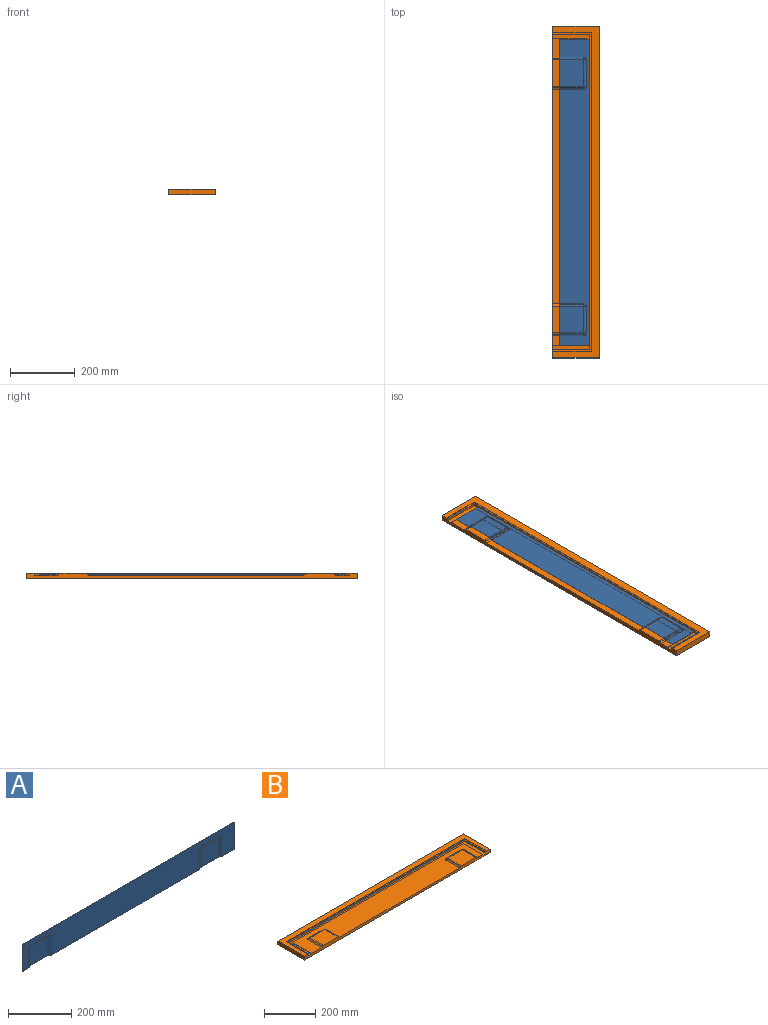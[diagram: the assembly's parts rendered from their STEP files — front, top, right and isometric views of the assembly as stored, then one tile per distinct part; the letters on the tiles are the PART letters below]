
ASSEMBLY  parts=2 mates=1
PART A: 50 faces, bbox 946.3x6.2x105 mm
  f0: plane 105x0.75mm, normal (-1,0,0), area 78.8mm2, adj f1,f2,f3,f4
  f1: plane 946.3x105mm, normal (0,1,0), area 82973.2mm2, adj f0,f2,f4,f5,f6,f7,f8,f9
  f2: plane 946.3x6.15mm, normal (0,0,-1), area 715.9mm2, adj f0,f1,f3,f5,f6,f10,f11,f15
  f3: plane 946.3x105mm, normal (0,-1,0), area 82973.2mm2, adj f0,f2,f4,f5,f29,f33,f34,f37
  f4: plane 946.3x0.75mm, normal (0,0,1), area 709.7mm2, adj f0,f1,f3,f5
  f5: plane 105x0.75mm, normal (1,0,0), area 78.8mm2, adj f1,f2,f3,f4
  f6: cylinder r=5mm len=73.6mm, axis (0,0,-1), area 402.2mm2, adj f1,f2,f7,f21
  f7: torus R=8.88mm, axis (0,-1,0), area 55mm2, adj f1,f6,f8,f22
  f8: cylinder r=5mm len=82mm, axis (-1,0,0), area 448mm2, adj f1,f7,f9,f23
  f9: torus R=8.88mm, axis (0,-1,0), area 55mm2, adj f1,f8,f10,f24
  f10: cylinder r=5mm len=73.6mm, axis (0,0,1), area 402.2mm2, adj f1,f2,f9,f19
  f11: cylinder r=5mm len=73.6mm, axis (0,0,-1), area 402.2mm2, adj f1,f2,f12,f18
  f12: torus R=8.88mm, axis (0,-1,0), area 55mm2, adj f1,f11,f13,f25
  f13: cylinder r=5mm len=82mm, axis (-1,0,0), area 448mm2, adj f1,f12,f14,f26
  f14: torus R=8.88mm, axis (0,-1,0), area 55mm2, adj f1,f13,f15,f27
  f15: cylinder r=5mm len=73.6mm, axis (0,0,1), area 402.2mm2, adj f1,f2,f14,f16
  f16: cylinder r=5mm len=73.6mm, axis (0,0,-1), area 402.2mm2, adj f2,f15,f17,f27
  f17: plane 82x73.6mm, normal (0,1,0), area 6035.2mm2, adj f2,f16,f18,f26
  f18: cylinder r=5mm len=73.6mm, axis (0,0,1), area 402.2mm2, adj f2,f11,f17,f25
  f19: cylinder r=5mm len=73.6mm, axis (0,0,-1), area 402.2mm2, adj f2,f10,f20,f24
  f20: plane 82x73.6mm, normal (0,1,0), area 6035.2mm2, adj f2,f19,f21,f23
  f21: cylinder r=5mm len=73.6mm, axis (0,0,1), area 402.2mm2, adj f2,f6,f20,f22
  f22: sphere r=5mm, area 21.2mm2, adj f7,f21,f23
  f23: cylinder r=5mm len=82mm, axis (-1,0,0), area 448mm2, adj f8,f20,f22,f24
  f24: sphere r=5mm, area 21.2mm2, adj f9,f19,f23
  f25: sphere r=5mm, area 21.2mm2, adj f12,f18,f26
  f26: cylinder r=5mm len=82mm, axis (-1,0,0), area 448mm2, adj f13,f17,f25,f27
  f27: sphere r=5mm, area 21.2mm2, adj f14,f16,f26
  f28: cylinder r=4.25mm len=82mm, axis (-1,0,0), area 380.8mm2, adj f29,f30,f31,f32
  f29: cylinder r=5.75mm len=82mm, axis (-1,0,0), area 515.3mm2, adj f3,f28,f33,f34
  f30: sphere r=4.25mm, area 15.3mm2, adj f28,f33,f35
  f31: plane 82x73.6mm, normal (0,-1,0), area 6035.2mm2, adj f2,f28,f35,f36
  f32: sphere r=4.25mm, area 15.3mm2, adj f28,f34,f36
  f33: torus R=8.88mm, axis (0,-1,0), area 59.6mm2, adj f3,f29,f30,f37
  f34: torus R=8.88mm, axis (0,-1,0), area 59.6mm2, adj f3,f29,f32,f38
  f35: cylinder r=4.25mm len=73.6mm, axis (0,0,-1), area 341.8mm2, adj f2,f30,f31,f37
  f36: cylinder r=4.25mm len=73.6mm, axis (0,0,1), area 341.8mm2, adj f2,f31,f32,f38
  f37: cylinder r=5.75mm len=73.6mm, axis (0,0,1), area 462.5mm2, adj f2,f3,f33,f35
  f38: cylinder r=5.75mm len=73.6mm, axis (0,0,-1), area 462.5mm2, adj f2,f3,f34,f36
  f39: cylinder r=4.25mm len=82mm, axis (-1,0,0), area 380.8mm2, adj f40,f41,f42,f43
  f40: cylinder r=5.75mm len=82mm, axis (-1,0,0), area 515.3mm2, adj f3,f39,f44,f45
  f41: sphere r=4.25mm, area 15.3mm2, adj f39,f45,f46
  f42: plane 82x73.6mm, normal (0,-1,0), area 6035.2mm2, adj f2,f39,f46,f47
  f43: sphere r=4.25mm, area 15.3mm2, adj f39,f44,f47
  f44: torus R=8.88mm, axis (0,-1,0), area 59.6mm2, adj f3,f40,f43,f48
  f45: torus R=8.88mm, axis (0,-1,0), area 59.6mm2, adj f3,f40,f41,f49
  f46: cylinder r=4.25mm len=73.6mm, axis (0,0,-1), area 341.8mm2, adj f2,f41,f42,f49
  f47: cylinder r=4.25mm len=73.6mm, axis (0,0,1), area 341.8mm2, adj f2,f42,f43,f48
  f48: cylinder r=5.75mm len=73.6mm, axis (0,0,-1), area 462.5mm2, adj f2,f3,f44,f47
  f49: cylinder r=5.75mm len=73.6mm, axis (0,0,1), area 462.5mm2, adj f2,f3,f45,f46
PART B: 40 faces, bbox 1026.3x145x18.4 mm
  f0: plane 976.3x115mm, normal (0,0,1), area 12913mm2, adj f4,f7,f8,f9,f12,f13,f14
  f1: plane 946.3x105mm, normal (0,0,1), area 82966.5mm2, adj f4,f7,f8,f9,f30,f31,f32,f33
  f2: plane 1026.3x18.4mm, normal (0,1,0), area 18883.9mm2, adj f3,f5,f6,f19
  f3: plane 145x18.4mm, normal (-1,0,0), area 2668mm2, adj f2,f4,f6,f19
  f4: plane 1026.3x18.4mm, normal (0,-1,0), area 13541mm2, adj f0,f1,f3,f5,f6,f7,f9,f10
  f5: plane 145x18.4mm, normal (1,0,0), area 2668mm2, adj f2,f4,f6,f19
  f6: plane 1026.3x145mm, normal (0,0,-1), area 148813.5mm2, adj f2,f3,f4,f5
  f7: plane 105x2mm, normal (1,0,0), area 210mm2, adj f0,f1,f4,f8
  f8: plane 946.3x2mm, normal (0,1,0), area 1892.6mm2, adj f0,f1,f7,f9
  f9: plane 105x2mm, normal (-1,0,0), area 210mm2, adj f0,f1,f4,f8
  f10: plane 82x73.6mm, normal (0,0,1), area 6035.2mm2, adj f4,f25,f27,f28
  f11: plane 82x73.6mm, normal (0,0,1), area 6035.2mm2, adj f4,f20,f22,f23
  f12: plane 115x7.4mm, normal (1,0,0), area 851mm2, adj f0,f4,f13,f15
  f13: plane 976.3x7.4mm, normal (0,-1,0), area 7224.6mm2, adj f0,f12,f14,f15
  f14: plane 115x7.4mm, normal (-1,0,0), area 851mm2, adj f0,f4,f13,f15
  f15: plane 986.3x120mm, normal (0,0,1), area 6081.5mm2, adj f4,f12,f13,f14,f16,f17,f18
  f16: plane 120x1mm, normal (1,0,0), area 120mm2, adj f4,f15,f17,f19
  f17: plane 986.3x1mm, normal (0,-1,0), area 986.3mm2, adj f15,f16,f18,f19
  f18: plane 120x1mm, normal (-1,0,0), area 120mm2, adj f4,f15,f17,f19
  f19: plane 1026.3x145mm, normal (0,0,1), area 30457.5mm2, adj f2,f3,f4,f5,f16,f17,f18
  f20: cylinder r=4.25mm len=74.03mm, axis (0,1,0), area 342.8mm2, adj f4,f11,f21,f30
  f21: bspline ~3.98x3.98mm, area 8.1mm2, adj f20,f22,f31
  f22: cylinder r=4.25mm len=82.85mm, axis (-1,0,0), area 382.8mm2, adj f11,f21,f24,f33
  f23: cylinder r=4.25mm len=74.03mm, axis (0,1,0), area 342.8mm2, adj f4,f11,f24,f32
  f24: bspline ~3.98x3.98mm, area 8.1mm2, adj f22,f23,f34
  f25: cylinder r=4.25mm len=74.03mm, axis (0,1,0), area 342.8mm2, adj f4,f10,f26,f35
  f26: bspline ~3.98x3.98mm, area 8.1mm2, adj f25,f28,f36
  f27: cylinder r=4.25mm len=74.03mm, axis (0,1,0), area 342.8mm2, adj f4,f10,f29,f38
  f28: cylinder r=4.25mm len=82.85mm, axis (-1,0,0), area 382.8mm2, adj f10,f26,f29,f37
  f29: bspline ~3.98x3.98mm, area 8.1mm2, adj f27,f28,f39
  f30: cylinder r=5.75mm len=74.03mm, axis (0,1,0), area 465.1mm2, adj f1,f4,f20,f31
  f31: bspline ~9.41x9.1mm, area 55.3mm2, adj f1,f21,f30,f33
  f32: cylinder r=5.75mm len=74.03mm, axis (0,1,0), area 465.1mm2, adj f1,f4,f23,f34
  f33: cylinder r=5.75mm len=82.85mm, axis (-1,0,0), area 520.6mm2, adj f1,f22,f31,f34
  f34: bspline ~9.41x9.1mm, area 55.3mm2, adj f1,f24,f32,f33
  f35: cylinder r=5.75mm len=74.03mm, axis (0,1,0), area 465.1mm2, adj f1,f4,f25,f36
  f36: bspline ~9.41x9.1mm, area 55.3mm2, adj f1,f26,f35,f37
  f37: cylinder r=5.75mm len=82.85mm, axis (-1,0,0), area 520.6mm2, adj f1,f28,f36,f39
  f38: cylinder r=5.75mm len=74.03mm, axis (0,1,0), area 465.1mm2, adj f1,f4,f27,f39
  f39: bspline ~9.41x9.1mm, area 55.3mm2, adj f1,f29,f37,f38
PLACE A rot(axis=(0.58,0.58,0.58),120deg) t=(474.35,-276.67,-138.28)mm
PLACE B rot(axis=(0,0,-1),90deg) t=(597.15,667.11,-136.53)mm fixed
MATE slider A.f19 <-> B.f23  axis (-1,0,0) through (510.15,-199.67,-123.38)mm
